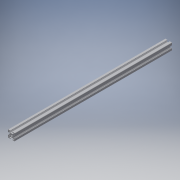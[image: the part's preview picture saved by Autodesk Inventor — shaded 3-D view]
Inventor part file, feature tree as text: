
AUTODESK INVENTOR PART (.ipt)
format: ipt  version: 2017 (Build 210142000, 142)  size: 307,200 bytes
history: native  units: in
note: dims shown in document units (in); Inventor stores cm internally (conversion verified against a paired STEP export)
features: other x3, extrude x1, sketch x1
ambient origin geometry x8: Origin, YZ Plane, XZ Plane, XY Plane, X Axis, Y Axis, Z Axis, Center Point
bodies: Solid1 (feature_tree)
feature tree (5):
  other  "Blocks"
  extrude  "Extrusion1"  [1 undecoded]
  sketch  "Sketch1"  dims[d1=0.0in]
  other  "20x20"
  other  "20x20:1"
note: 1 required parameter value undecoded (feature->parameter linkage not recoverable at this tier; creation-order binding heuristic only, values carry confidence <= 0.55)
